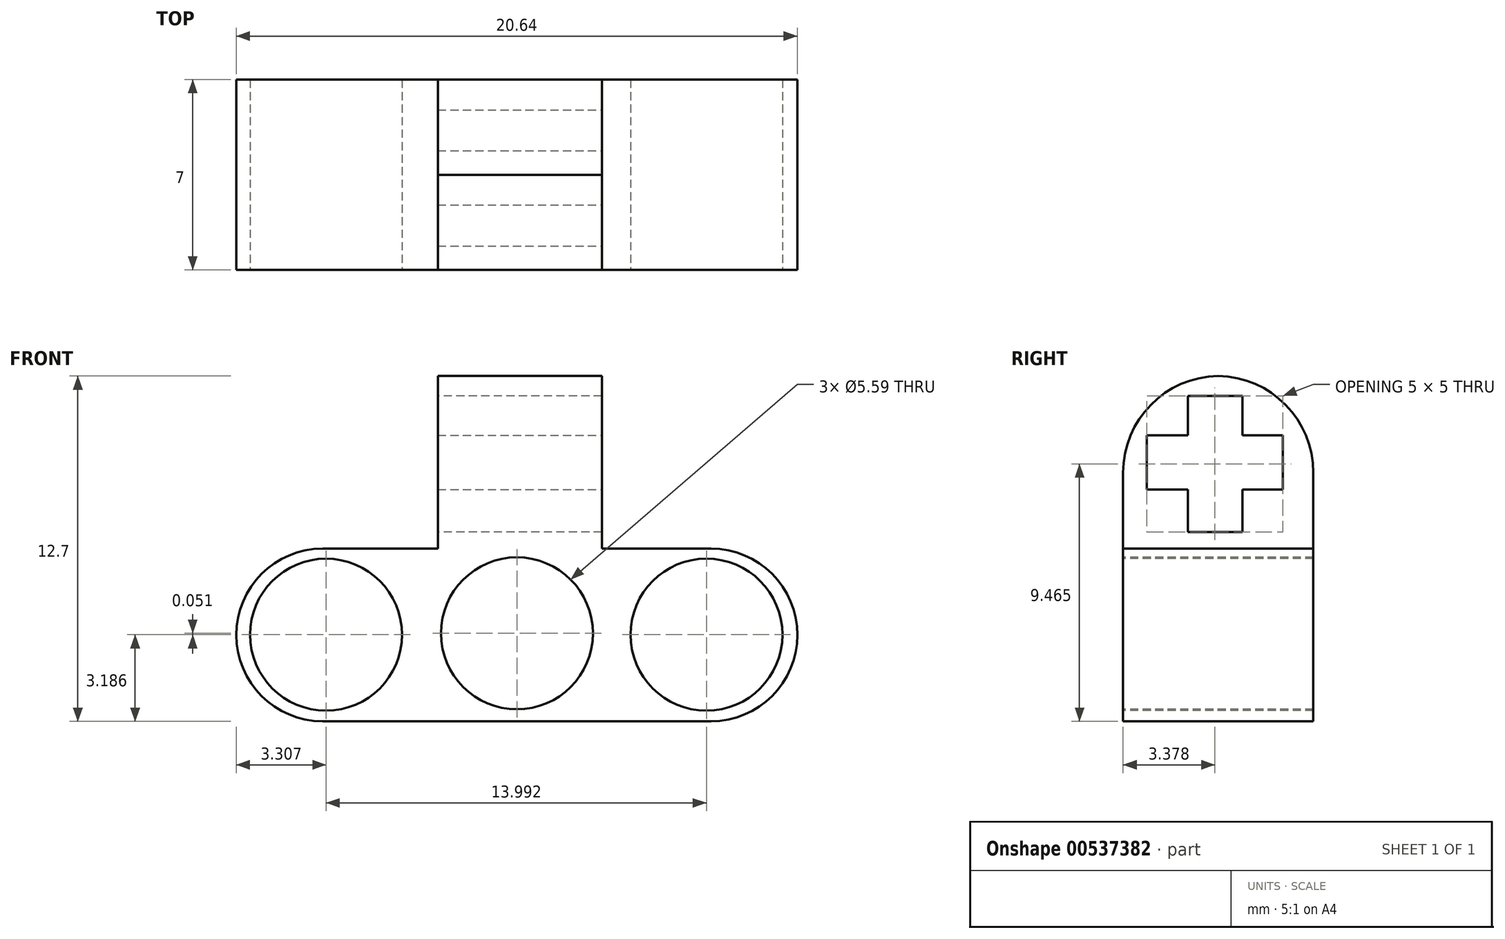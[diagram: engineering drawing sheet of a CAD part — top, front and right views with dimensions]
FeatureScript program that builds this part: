
annotation { "Feature Type Name" : "Feature", "Feature Type Description" : "" }
export const myFeature = defineFeature(function(context is Context, id is Id, definition is map)
    precondition{}
    {
        {
            var Q0;
            Q0=qCreatedBy(makeId("Top.planeOp"),FACE);
            var sketch = newSketch(context, id + "F0", { "sketchPlane" : qUnion([Q0])});
            skLineSegment(sketch, "E0.bottom", {"start": v(-8.74, -9.01) * mm, "end": v(11.9, -9.01) * mm});
            skLineSegment(sketch, "E0.top", {"start": v(-8.74, -16.01) * mm, "end": v(11.9, -16.01) * mm});
            skLineSegment(sketch, "E0.left", {"start": v(-8.74, -9.01) * mm, "end": v(-8.74, -16.01) * mm});
            skLineSegment(sketch, "E0.right", {"start": v(11.9, -9.01) * mm, "end": v(11.9, -16.01) * mm});
            skSolve(sketch);
        }
        {
            var Q0;
            Q0=makeQuery(id+"F0.imprint","IMPRINT",FACE,{"disambiguationData":[TD([[makeQuery(id+"F0.imprint","IMPRINT",EDGE,{"derivedFrom":sQuery(id+"F0.wireOp",EDGE,"E0.bottom")}),-1.0]])]});
            extrude(context, id + "F1", {"entities" : qUnion([Q0]), "depth" : 6.35 * mm, "offsetDistance" : 25.4 * mm});
        }
        {
            var Q0;
            Q0=makeQuery(id+"F1.opExtrude","SWEPT_FACE",FACE,{"disambiguationData":[OSD([sQuery(id+"F0.wireOp",EDGE,"E0.top")])]});
            var sketch = newSketch(context, id + "F2", { "sketchPlane" : qUnion([Q0])});
            skCircle(sketch, "E1", {"center": v(-5.43, 3.19) * mm, "radius": 2.8 * mm});
            skCircle(sketch, "E2", {"center": v(1.59, 3.24) * mm, "radius": 2.8 * mm});
            skCircle(sketch, "E3", {"center": v(8.56, 3.19) * mm, "radius": 2.8 * mm});
            skPoint(sketch, "E4.center", {"position": v(0, 0) * mm});
            skSolve(sketch);
        }
        {
            var Q0;
            Q0 = qSketchRegion(id + "F2", true);
            extrude(context, id + "F3", {"entities" : qUnion([Q0]), "operationType" : NewBodyOperationType.REMOVE, "oppositeDirection" : true, "depth" : 8 * mm, "offsetDistance" : 25.4 * mm});
        }
        {
            var Q0;
            Q0=makeQuery(id+"F1.opExtrude","CAP_EDGE",EDGE,{"disambiguationData":[OSD([sQuery(id+"F0.wireOp",EDGE,"E0.right")])],"isStart":false});
            var Q1;
            Q1=makeQuery(id+"F1.opExtrude","CAP_EDGE",EDGE,{"disambiguationData":[OSD([sQuery(id+"F0.wireOp",EDGE,"E0.right")])],"isStart":true});
            var Q2;
            Q2=makeQuery(id+"F1.opExtrude","CAP_EDGE",EDGE,{"disambiguationData":[OSD([sQuery(id+"F0.wireOp",EDGE,"E0.left")])],"isStart":false});
            var Q3;
            Q3=makeQuery(id+"F1.opExtrude","CAP_EDGE",EDGE,{"disambiguationData":[OSD([sQuery(id+"F0.wireOp",EDGE,"E0.left")])],"isStart":true});
            fillet(context, id + "F4", {"entities" : qUnion([Q0, Q1, Q2, Q3]), "radius" : 3.17 * mm, "tangentPropagation" : true, "allowEdgeOverflow" : false});
        }
        {
            var Q0;
            Q0=makeQuery(id+"F1.opExtrude","CAP_FACE",FACE,{"disambiguationData":[OSD([sQuery(id+"F0.wireOp",EDGE,"E0.bottom"),sQuery(id+"F0.wireOp",EDGE,"E0.top"),sQuery(id+"F0.wireOp",EDGE,"E0.left"),sQuery(id+"F0.wireOp",EDGE,"E0.right")])],"isStart":false});
            var sketch = newSketch(context, id + "F5", { "sketchPlane" : qUnion([Q0])});
            skLineSegment(sketch, "E5", {"start": v(1.58, -16.01) * mm, "end": v(1.58, -15.26) * mm, "construction": true});
            skLineSegment(sketch, "E6", {"start": v(-1.32, -9.01) * mm, "end": v(-1.32, -16.01) * mm});
            skLineSegment(sketch, "E7", {"start": v(4.72, -9.01) * mm, "end": v(4.72, -16.01) * mm});
            skLineSegment(sketch, "E8", {"start": v(4.72, -16.01) * mm, "end": v(-1.32, -16.01) * mm});
            skLineSegment(sketch, "E9", {"start": v(4.72, -9.01) * mm, "end": v(-1.32, -9.01) * mm});
            skSolve(sketch);
        }
        {
            var Q0;
            Q0=makeQuery(id+"F5.imprint","IMPRINT",FACE,{"disambiguationData":[TD([[makeQuery(id+"F5.imprint","IMPRINT",EDGE,{"derivedFrom":sQuery(id+"F5.wireOp",EDGE,"E6")}),1.0]])]});
            extrude(context, id + "F6", {"entities" : qUnion([Q0]), "operationType" : NewBodyOperationType.ADD, "depth" : 6.35 * mm, "offsetDistance" : 25.4 * mm});
        }
        {
            var Q0;
            Q0=makeQuery(id+"F6.opExtrude","CAP_EDGE",EDGE,{"disambiguationData":[OSD([sQuery(id+"F5.wireOp",EDGE,"E8")])],"isStart":false});
            var Q1;
            Q1=makeQuery(id+"F6.opExtrude","CAP_EDGE",EDGE,{"disambiguationData":[OSD([sQuery(id+"F5.wireOp",EDGE,"E9")])],"isStart":false});
            fillet(context, id + "F7", {"entities" : qUnion([Q0, Q1]), "radius" : 3.56 * mm, "tangentPropagation" : true, "allowEdgeOverflow" : false});
        }
        {
            var Q0;
            Q0=makeQuery(id+"F6.opExtrude","SWEPT_FACE",FACE,{"disambiguationData":[OSD([sQuery(id+"F5.wireOp",EDGE,"E6")])]});
            var sketch = newSketch(context, id + "F8", { "sketchPlane" : qUnion([Q0])});
            skLineSegment(sketch, "E10.bottom", {"start": v(13.62, 11.97) * mm, "end": v(11.62, 11.97) * mm});
            skLineSegment(sketch, "E10.top", {"start": v(13.62, 6.97) * mm, "end": v(11.62, 6.97) * mm});
            skLineSegment(sketch, "E10.left", {"start": v(13.62, 11.97) * mm, "end": v(13.62, 6.97) * mm});
            skLineSegment(sketch, "E10.right", {"start": v(11.62, 11.97) * mm, "end": v(11.62, 6.97) * mm});
            skSolve(sketch);
        }
        {
            var Q0;
            Q0 = qSketchRegion(id + "F8", true);
            extrude(context, id + "F9", {"entities" : qUnion([Q0]), "operationType" : NewBodyOperationType.REMOVE, "oppositeDirection" : true, "depth" : 6.35 * mm, "offsetDistance" : 25.4 * mm});
        }
        {
            var Q0;
            Q0=makeQuery(id+"F6.opExtrude","SWEPT_FACE",FACE,{"disambiguationData":[OSD([sQuery(id+"F5.wireOp",EDGE,"E7")])]});
            var sketch = newSketch(context, id + "F10", { "sketchPlane" : qUnion([Q0])});
            skLineSegment(sketch, "E11.bottom", {"start": v(-15.13, 10.52) * mm, "end": v(-10.13, 10.52) * mm});
            skLineSegment(sketch, "E11.top", {"start": v(-15.13, 8.52) * mm, "end": v(-10.13, 8.52) * mm});
            skLineSegment(sketch, "E11.left", {"start": v(-15.13, 10.52) * mm, "end": v(-15.13, 8.52) * mm});
            skLineSegment(sketch, "E11.right", {"start": v(-10.13, 10.52) * mm, "end": v(-10.13, 8.52) * mm});
            skSolve(sketch);
        }
        {
            var Q0;
            {var subQ0=sQuery(id+"F10.wireOp",EDGE,"E11.left");Q0=makeQuery(id+"F10.imprint","IMPRINT",FACE,{"disambiguationData":[TD([[makeQuery(id+"F10.imprint","IMPRINT",EDGE,{"derivedFrom":subQ0}),1.0]])]});}
            var Q1;
            {var subQ0=sQuery(id+"F10.wireOp",EDGE,"E11.right");Q1=makeQuery(id+"F10.imprint","IMPRINT",FACE,{"disambiguationData":[TD([[makeQuery(id+"F10.imprint","IMPRINT",EDGE,{"derivedFrom":subQ0}),-1.0]])]});}
            var Q2;
            {var subQ1=makeQuery(id+"F6.opExtrude","SWEPT_FACE",FACE,{"disambiguationData":[OSD([sQuery(id+"F5.wireOp",EDGE,"E7")])]});var subQ6=makeQuery(id+"F9.boolean.opBoolean","INTERSECT",EDGE,{"derivedFrom":[subQ1,makeQuery(id+"F9.opExtrude","SWEPT_FACE",FACE,{"disambiguationData":[OSD([sQuery(id+"F8.wireOp",EDGE,"E10.bottom")])]})]});Q2=makeQuery(id+"F10.imprint","IMPRINT",FACE,{"disambiguationData":[TD([[makeQuery(id+"F10.imprint","IMPRINT",EDGE,{"derivedFrom":subQ6}),1.0]])]});}
            var Q3;
            {var subQ1=makeQuery(id+"F6.opExtrude","SWEPT_FACE",FACE,{"disambiguationData":[OSD([sQuery(id+"F5.wireOp",EDGE,"E7")])]});var subQ6=makeQuery(id+"F9.boolean.opBoolean","INTERSECT",EDGE,{"derivedFrom":[subQ1,makeQuery(id+"F9.opExtrude","SWEPT_FACE",FACE,{"disambiguationData":[OSD([sQuery(id+"F8.wireOp",EDGE,"E10.top")])]})]});Q3=makeQuery(id+"F10.imprint","IMPRINT",FACE,{"disambiguationData":[TD([[makeQuery(id+"F10.imprint","IMPRINT",EDGE,{"derivedFrom":subQ6}),-1.0]])]});}
            extrude(context, id + "F11", {"entities" : qUnion([Q0, Q1, Q2, Q3]), "operationType" : NewBodyOperationType.REMOVE, "oppositeDirection" : true, "depth" : 6.35 * mm, "offsetDistance" : 25.4 * mm});
        }
    });
